# Revit family: Haworth_BuzziPleat_Ripple_AP_PRELIMINARY
name_source: partatom
category: Furniture
revit_build: Autodesk Revit 2018 (Build: 20170223_1515(x64)
units: mm (PartAtom-declared; Revit-internal decimal feet)

## family parameters
Cut with Voids When Loaded = No
Host = Face
Room Calculation Point = No
Shared = No

## types (2) — shared parameters
Assembly Code = E2020200
Description = Haworth - BuzziPleat - Ripple
Manufacturer = Haworth
Max. Cable Length = 5000 mm
Min. Cable Length = 254 mm  [stored 0.833333 ft]
Model = Buzzi Pleat
Note = Verify Final Dim. w/ Haworth
Trim Finish = Haworth _ Paint _ Collection Black
URL = https://www.haworth.com
URL - Product = https://www.haworth.com
Warranty = https://www.haworth.com
zero-valued in all types: Default Elevation

## per-type parameters (varying)
| type | Actual Depth | Actual Height | Actual Width | Large | Medium |
| Large | 1500 mm | 195 mm | 1500 mm | Yes | No |
| Medium | 1000 mm  [stored 3.28084 ft] | 132 mm | 1000 mm  [stored 3.28084 ft] | No | Yes |

note: [stored X ft] marks values corroborated as IEEE doubles in the binary element streams (Revit-internal decimal feet)

## geometry (parser evidence)
native form markers: Blend x4, Sweep x19
no freeform markers — native parametric forms only
